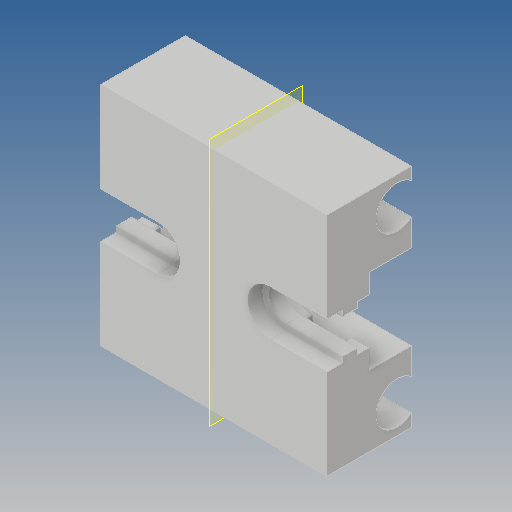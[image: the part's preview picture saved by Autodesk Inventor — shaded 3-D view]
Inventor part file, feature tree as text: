
AUTODESK INVENTOR PART (.ipt)
format: ipt  version: 2018 (Build 220112000, 112)  size: 236,032 bytes
history: native  units: mm
features: extrude x6, sketch x6, other x1, plane x1, mirror x1
ambient origin geometry x8: Origin, YZ Plane, XZ Plane, XY Plane, X Axis, Y Axis, Z Axis, Center Point
bodies: Solid1 (feature_tree)
feature tree (15):
  other  "<userpath>\OneDrive\Objet3D\3DPrinter\Parameters.xlsx"
  extrude  "Extrusion1"  Depth=80.0mm
  extrude  "Extrusion2"  Depth=15.0mm
  extrude  "Extrusion3"  Depth=12.2mm
  extrude  "Extrusion4"  Depth=16.2mm
  extrude  "Extrusion5"  Depth=5.5mm TaperAngle=0.0deg
  extrude  "Extrusion6"  Depth=4.0mm TaperAngle=0.0deg
  plane  "Work Plane1"
  mirror  "Mirror1"
  sketch  "Sketch1"  dims[d0=80.0mm d1=80.0mm]
  sketch  "Sketch2"  dims[d2=15.0mm d3=0.0mm d7=40.0mm]
  sketch  "Sketch3"  dims[d8=20.0mm d9=12.2mm]
  sketch  "Sketch4"  dims[d10=10.0mm d11=0.0mm d12=16.2mm]
  sketch  "Sketch5"  dims[d13=4.0mm d14=0.0mm d15=5.5mm d16=0.0mm]
  sketch  "Sketch6"  dims[d17=13.8mm d18=4.0mm d19=0.0mm d20=16.2mm d21=8.1mm d22=25.0mm d23=25.0mm d24=15.0mm d25=15.0mm d29=15.0mm d30=5.0mm d31=5.0mm d32=15.0mm d33=5.0mm d34=5.0mm d35=80.0mm d36=0.0mm d37=0.0mm d38=15.0mm d39=15.0mm d40=60.0mm d41=10.0mm d42=10.0mm]
